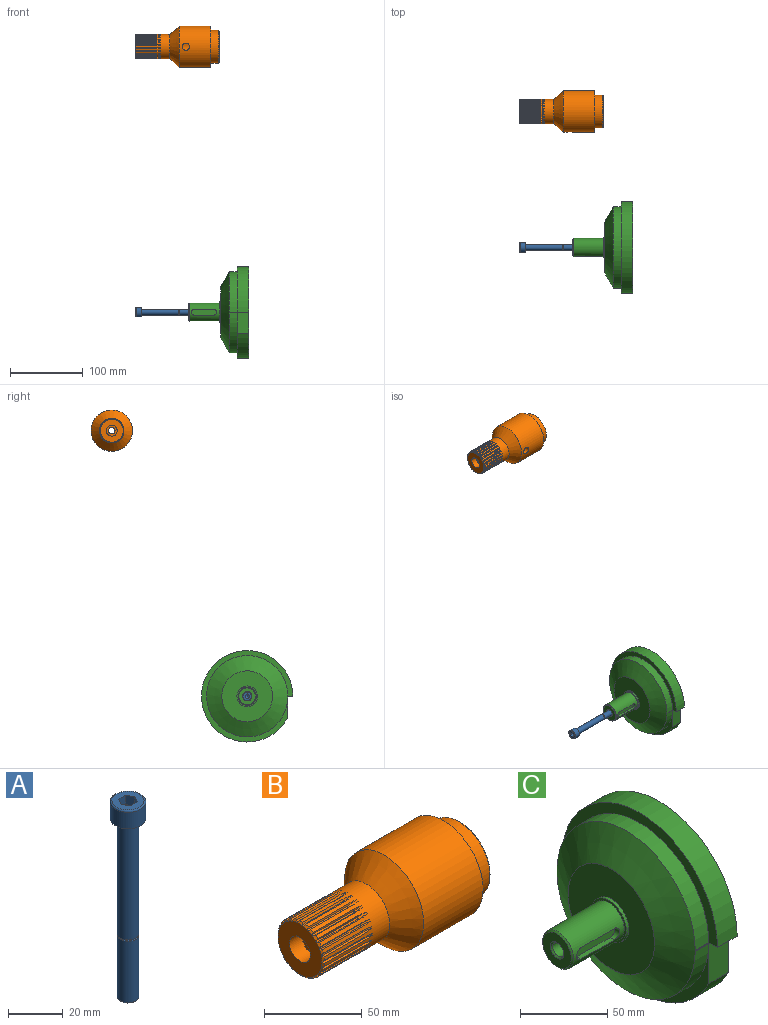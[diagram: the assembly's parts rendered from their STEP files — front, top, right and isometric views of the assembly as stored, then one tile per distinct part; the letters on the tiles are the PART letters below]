
ASSEMBLY  parts=3 mates=3
PART A: 17 faces, bbox 14.1x14.1x88 mm
  f0: cylinder r=6.5mm len=13mm, axis (0,0,-1), area 300.2mm2, adj f1,f16
  f1: torus R=5.85mm, axis (0,0,-1), area 40.2mm2, adj f0,f15
  f2: cone r=3.73mm half-angle=45deg, axis (0,0,1), area 17.9mm2, adj f3,f14
  f3: cylinder r=4mm len=27.46mm, axis (0,0,-1), area 690.1mm2, adj f2,f13
  f4: cone r=3.73mm half-angle=45deg, axis (0,0,1), area 17.9mm2, adj f5,f13
  f5: cylinder r=4mm len=51.46mm, axis (0,0,-1), area 1293.3mm2, adj f4,f16
  f6: cone r=1.73mm half-angle=60deg, axis (0,0,1), area 36mm2, adj f7,f8,f9,f10,f11,f12
  f7: plane 4.4x3mm, normal (0.87,0.5,0), area 14.5mm2, adj f6,f8,f12,f15
  f8: plane 4.4x3.46mm, normal (0,1,0), area 14.5mm2, adj f6,f7,f9,f15
  f9: plane 4.4x3mm, normal (-0.87,0.5,0), area 14.5mm2, adj f6,f8,f10,f15
  f10: plane 4.4x3mm, normal (-0.87,-0.5,0), area 14.5mm2, adj f6,f9,f11,f15
  f11: plane 4.31x3.46mm, normal (0,-1,0), area 14.5mm2, adj f6,f10,f12,f15
  f12: plane 4.4x3mm, normal (0.87,-0.5,0), area 14.5mm2, adj f6,f7,f11,f15
  f13: plane 8x8mm, normal (0,0,1), area 12.7mm2, adj f3,f4
  f14: plane 6.92x6.92mm, normal (0,0,-1), area 37.6mm2, adj f2
  f15: plane 11.7x11.7mm, normal (0,0,1), area 76.3mm2, adj f1,f7,f8,f9,f10,f11,f12
  f16: plane 13x13mm, normal (0,0,-1), area 82.5mm2, adj f0,f5
PART B: 200 faces, bbox 116x57x57 mm
  f0: cylinder r=12.5mm len=52.3mm, axis (-1,0,0), area 3694.3mm2, adj f2,f3,f36,f198,f199
  f1: cylinder r=28.5mm len=57mm, axis (-1,0,0), area 7621.6mm2, adj f32,f33,f198
  f2: plane 43.01x4.16mm, normal (0,-1,0), area 178.5mm2, adj f0,f35,f41,f198,f199
  f3: plane 43.01x4.16mm, normal (0,1,0), area 178.5mm2, adj f0,f35,f41,f198,f199
  f4: cone r=15.88mm half-angle=45deg, axis (1,0,0), area 3.5mm2, adj f30,f31,f177,f196
  f5: cone r=15.88mm half-angle=45deg, axis (1,0,0), area 3.5mm2, adj f30,f31,f190,f195
  f6: cone r=15.88mm half-angle=45deg, axis (1,0,0), area 3.5mm2, adj f30,f31,f87,f184
  f7: cone r=15.88mm half-angle=45deg, axis (1,0,0), area 3.5mm2, adj f30,f31,f178,f183
  f8: cone r=15.88mm half-angle=45deg, axis (1,0,0), area 3.5mm2, adj f30,f31,f153,f172
  f9: cone r=15.88mm half-angle=45deg, axis (1,0,0), area 3.5mm2, adj f30,f31,f166,f171
  f10: cone r=15.88mm half-angle=45deg, axis (1,0,0), area 3.5mm2, adj f30,f31,f160,f189
  f11: cone r=15.88mm half-angle=45deg, axis (1,0,0), area 3.5mm2, adj f30,f31,f154,f159
  f12: cone r=15.88mm half-angle=45deg, axis (1,0,0), area 3.5mm2, adj f30,f31,f141,f148
  f13: cone r=15.88mm half-angle=45deg, axis (1,0,0), area 3.5mm2, adj f30,f31,f123,f142
  f14: cone r=15.88mm half-angle=45deg, axis (1,0,0), area 3.5mm2, adj f30,f31,f129,f136
  f15: cone r=15.88mm half-angle=45deg, axis (1,0,0), area 3.5mm2, adj f30,f31,f130,f147
  f16: cone r=15.88mm half-angle=45deg, axis (1,0,0), area 3.5mm2, adj f30,f31,f117,f124
  f17: cone r=15.88mm half-angle=45deg, axis (1,0,0), area 3.5mm2, adj f30,f31,f105,f118
  f18: cone r=15.88mm half-angle=45deg, axis (1,0,0), area 3.5mm2, adj f30,f31,f112,f165
  f19: cone r=15.88mm half-angle=45deg, axis (1,0,0), area 3.5mm2, adj f30,f31,f106,f111
  f20: cone r=15.88mm half-angle=45deg, axis (1,0,0), area 3.5mm2, adj f30,f31,f45,f100
  f21: cone r=15.88mm half-angle=45deg, axis (1,0,0), area 3.5mm2, adj f30,f31,f81,f94
  f22: cone r=15.88mm half-angle=45deg, axis (1,0,0), area 3.5mm2, adj f30,f31,f88,f93
  f23: cone r=15.88mm half-angle=45deg, axis (1,0,0), area 3.5mm2, adj f30,f31,f75,f82
  f24: cone r=15.88mm half-angle=45deg, axis (1,0,0), area 3.5mm2, adj f30,f31,f57,f76
  f25: cone r=15.88mm half-angle=45deg, axis (1,0,0), area 3.5mm2, adj f30,f31,f63,f70
  f26: cone r=15.88mm half-angle=45deg, axis (1,0,0), area 3.5mm2, adj f30,f31,f64,f99
  f27: cone r=15.88mm half-angle=45deg, axis (1,0,0), area 3.5mm2, adj f30,f31,f51,f58
  f28: cone r=15.88mm half-angle=45deg, axis (1,0,0), area 3.5mm2, adj f30,f31,f52,f69
  f29: cylinder r=7.5mm len=15mm, axis (-1,0,0), area 424.1mm2, adj f30,f38
  f30: plane 31.75x31.75mm, normal (-1,0,0), area 615mm2, adj f4,f5,f6,f7,f8,f9,f10,f11
  f31: cylinder r=16.88mm len=47mm, axis (-1,0,0), area 3188.5mm2, adj f4,f5,f6,f7,f8,f9,f10,f11
  f32: cone r=28.5mm half-angle=41.8deg, axis (1,0,0), area 2486mm2, adj f1,f31
  f33: plane 57x57mm, normal (1,0,0), area 961.3mm2, adj f1,f34
  f34: cylinder r=22.5mm len=45mm, axis (-1,0,0), area 1555.1mm2, adj f33,f39
  f35: plane 43x43mm, normal (1,0,0), area 880.8mm2, adj f2,f3,f39,f41,f199
  f36: cone r=12.5mm half-angle=59deg, axis (1,0,0), area 498.5mm2, adj f0,f37
  f37: cylinder r=4.5mm len=49.19mm, axis (-1,0,0), area 1390.9mm2, adj f36,f38
  f38: plane 15x15mm, normal (-1,0,0), area 113.1mm2, adj f29,f37
  f39: cone r=22.5mm half-angle=45deg, axis (-1,0,0), area 195.5mm2, adj f34,f35
  f40: cone r=15.88mm half-angle=45deg, axis (1,0,0), area 3.5mm2, adj f30,f31,f46,f135
  f41: plane 43x8mm, normal (0,0,1), area 332.8mm2, adj f2,f3,f35,f198
  f42: cone r=15.3mm half-angle=59.4deg, axis (0,0.99,0.13), area 4.3mm2, adj f31,f44,f45
  f43: cone r=15.28mm half-angle=60.6deg, axis (0,-0.99,-0.13), area 4.3mm2, adj f31,f44,f46
  f44: torus R=32.14mm, axis (0,-0.99,-0.13), area 5.3mm2, adj f31,f42,f43,f47
  f45: plane 30.02x1.05mm, normal (0,0.92,-0.39), area 33.2mm2, adj f20,f31,f42,f47
  f46: plane 30.02x0.92mm, normal (0,-0.8,-0.6), area 33.2mm2, adj f31,f40,f43,f47
  f47: cylinder r=15.88mm len=30mm, axis (-1,0,0), area 27.8mm2, adj f30,f44,f45,f46
  f48: cone r=15.3mm half-angle=59.4deg, axis (0,0.67,-0.74), area 4.3mm2, adj f31,f50,f51
  f49: cone r=15.28mm half-angle=60.6deg, axis (0,-0.67,0.74), area 4.3mm2, adj f31,f50,f52
  f50: torus R=32.14mm, axis (0,-0.67,0.74), area 5.3mm2, adj f31,f48,f49,f53
  f51: plane 30.02x1.12mm, normal (0,0.2,-0.98), area 33.2mm2, adj f27,f31,f48,f53
  f52: plane 30.02x1.09mm, normal (0,-0.95,0.32), area 33.2mm2, adj f28,f31,f49,f53
  f53: cylinder r=15.88mm len=30mm, axis (-1,0,0), area 27.8mm2, adj f30,f50,f51,f52
  f54: cone r=15.3mm half-angle=59.4deg, axis (0,0.47,-0.88), area 4.3mm2, adj f31,f56,f57
  f55: cone r=15.28mm half-angle=60.6deg, axis (0,-0.47,0.88), area 4.3mm2, adj f31,f56,f58
  f56: torus R=32.14mm, axis (0,-0.47,0.88), area 5.3mm2, adj f31,f54,f55,f59
  f57: plane 30.02x1.14mm, normal (0,-0.04,-1), area 33.2mm2, adj f24,f31,f54,f59
  f58: plane 30.02x0.97mm, normal (0,-0.85,0.53), area 33.2mm2, adj f27,f31,f55,f59
  f59: cylinder r=15.88mm len=30mm, axis (-1,0,0), area 27.8mm2, adj f30,f56,f57,f58
  f60: cone r=15.3mm half-angle=59.4deg, axis (0,0.94,-0.34), area 4.3mm2, adj f31,f62,f63
  f61: cone r=15.28mm half-angle=60.6deg, axis (0,-0.94,0.34), area 4.3mm2, adj f31,f62,f64
  f62: torus R=32.14mm, axis (0,-0.94,0.34), area 5.3mm2, adj f31,f60,f61,f65
  f63: plane 30.02x0.89mm, normal (0,0.63,-0.77), area 33.2mm2, adj f25,f31,f60,f65
  f64: plane 30.02x1.13mm, normal (0,-0.99,-0.16), area 33.2mm2, adj f26,f31,f61,f65
  f65: cylinder r=15.88mm len=30mm, axis (-1,0,0), area 27.8mm2, adj f30,f62,f63,f64
  f66: cone r=15.3mm half-angle=59.4deg, axis (0,0.83,-0.56), area 4.3mm2, adj f31,f68,f69
  f67: cone r=15.28mm half-angle=60.6deg, axis (0,-0.83,0.56), area 4.3mm2, adj f31,f68,f70
  f68: torus R=32.14mm, axis (0,-0.83,0.56), area 5.3mm2, adj f31,f66,f67,f71
  f69: plane 30.02x1.03mm, normal (0,0.43,-0.9), area 33.2mm2, adj f28,f31,f66,f71
  f70: plane 30.02x1.14mm, normal (0,-1,0.08), area 33.2mm2, adj f25,f31,f67,f71
  f71: cylinder r=15.88mm len=30mm, axis (-1,0,0), area 27.8mm2, adj f30,f68,f69,f70
  f72: cone r=15.3mm half-angle=59.4deg, axis (0,0.25,-0.97), area 4.3mm2, adj f31,f74,f75
  f73: cone r=15.28mm half-angle=60.6deg, axis (0,-0.25,0.97), area 4.3mm2, adj f31,f74,f76
  f74: torus R=32.14mm, axis (0,-0.25,0.97), area 5.3mm2, adj f31,f72,f73,f77
  f75: plane 30.02x1.1mm, normal (0,-0.28,-0.96), area 33.2mm2, adj f23,f31,f72,f77
  f76: plane 30.02x0.83mm, normal (0,-0.69,0.72), area 33.2mm2, adj f24,f31,f73,f77
  f77: cylinder r=15.88mm len=30mm, axis (-1,0,0), area 27.8mm2, adj f30,f74,f75,f76
  f78: cone r=15.3mm half-angle=59.4deg, axis (0,0.01,-1), area 4.3mm2, adj f31,f80,f81
  f79: cone r=15.28mm half-angle=60.6deg, axis (0,-0.01,1), area 4.3mm2, adj f31,f80,f82
  f80: torus R=32.14mm, axis (0,-0.01,1), area 5.3mm2, adj f31,f78,f79,f83
  f81: plane 30.02x0.99mm, normal (0,-0.5,-0.87), area 33.2mm2, adj f21,f31,f78,f83
  f82: plane 30.02x0.99mm, normal (0,-0.5,0.87), area 33.2mm2, adj f23,f31,f79,f83
  f83: cylinder r=15.88mm len=30mm, axis (-1,0,0), area 27.8mm2, adj f30,f80,f81,f82
  f84: cone r=15.3mm half-angle=59.4deg, axis (0,-0.46,-0.89), area 4.3mm2, adj f31,f86,f87
  f85: cone r=15.28mm half-angle=60.6deg, axis (0,0.46,0.89), area 4.3mm2, adj f31,f86,f88
  f86: torus R=32.14mm, axis (0,0.46,0.89), area 5.3mm2, adj f31,f84,f85,f89
  f87: plane 30.02x0.97mm, normal (0,-0.85,-0.53), area 33.2mm2, adj f6,f31,f84,f89
  f88: plane 30.02x1.14mm, normal (0,-0.04,1), area 33.2mm2, adj f22,f31,f85,f89
  f89: cylinder r=15.88mm len=30mm, axis (-1,0,0), area 27.8mm2, adj f30,f86,f87,f88
  f90: cone r=15.3mm half-angle=59.4deg, axis (0,-0.23,-0.97), area 4.3mm2, adj f31,f92,f93
  f91: cone r=15.28mm half-angle=60.6deg, axis (0,0.23,0.97), area 4.3mm2, adj f31,f92,f94
  f92: torus R=32.14mm, axis (0,0.23,0.97), area 5.3mm2, adj f31,f90,f91,f95
  f93: plane 30.02x0.83mm, normal (0,-0.69,-0.72), area 33.2mm2, adj f22,f31,f90,f95
  f94: plane 30.02x1.1mm, normal (0,-0.28,0.96), area 33.2mm2, adj f21,f31,f91,f95
  f95: cylinder r=15.88mm len=30mm, axis (-1,0,0), area 27.8mm2, adj f30,f92,f93,f94
  f96: cone r=15.3mm half-angle=59.4deg, axis (0,0.99,-0.11), area 4.3mm2, adj f31,f98,f99
  f97: cone r=15.28mm half-angle=60.6deg, axis (0,-0.99,0.11), area 4.3mm2, adj f31,f98,f100
  f98: torus R=32.14mm, axis (0,-0.99,0.11), area 5.3mm2, adj f31,f96,f97,f101
  f99: plane 30.02x0.92mm, normal (0,0.8,-0.6), area 33.2mm2, adj f26,f31,f96,f101
  f100: plane 30.02x1.05mm, normal (0,-0.92,-0.39), area 33.2mm2, adj f20,f31,f97,f101
  f101: cylinder r=15.88mm len=30mm, axis (-1,0,0), area 27.8mm2, adj f30,f98,f99,f100
  f102: cone r=15.3mm half-angle=59.4deg, axis (0,-0.25,0.97), area 4.3mm2, adj f31,f104,f105
  f103: cone r=15.28mm half-angle=60.6deg, axis (0,0.25,-0.97), area 4.3mm2, adj f31,f104,f106
  f104: torus R=32.14mm, axis (0,0.25,-0.97), area 5.3mm2, adj f31,f102,f103,f107
  f105: plane 30.02x1.1mm, normal (0,0.28,0.96), area 33.2mm2, adj f17,f31,f102,f107
  f106: plane 30.02x0.83mm, normal (0,0.69,-0.72), area 33.2mm2, adj f19,f31,f103,f107
  f107: cylinder r=15.88mm len=30mm, axis (-1,0,0), area 27.8mm2, adj f30,f104,f105,f106
  f108: cone r=15.3mm half-angle=59.4deg, axis (0,-0.47,0.88), area 4.3mm2, adj f31,f110,f111
  f109: cone r=15.28mm half-angle=60.6deg, axis (0,0.47,-0.88), area 4.3mm2, adj f31,f110,f112
  f110: torus R=32.14mm, axis (0,0.47,-0.88), area 5.3mm2, adj f31,f108,f109,f113
  f111: plane 30.02x1.14mm, normal (0,0.04,1), area 33.2mm2, adj f19,f31,f108,f113
  f112: plane 30.02x0.97mm, normal (0,0.85,-0.53), area 33.2mm2, adj f18,f31,f109,f113
  f113: cylinder r=15.88mm len=30mm, axis (-1,0,0), area 27.8mm2, adj f30,f110,f111,f112
  f114: cone r=15.3mm half-angle=59.4deg, axis (0,-0.01,1), area 4.3mm2, adj f31,f116,f117
  f115: cone r=15.28mm half-angle=60.6deg, axis (0,0.01,-1), area 4.3mm2, adj f31,f116,f118
  f116: torus R=32.14mm, axis (0,0.01,-1), area 5.3mm2, adj f31,f114,f115,f119
  f117: plane 30.02x0.99mm, normal (0,0.5,0.87), area 33.2mm2, adj f16,f31,f114,f119
  f118: plane 30.02x0.99mm, normal (0,0.5,-0.87), area 33.2mm2, adj f17,f31,f115,f119
  f119: cylinder r=15.88mm len=30mm, axis (-1,0,0), area 27.8mm2, adj f30,f116,f117,f118
  f120: cone r=15.3mm half-angle=59.4deg, axis (0,0.23,0.97), area 4.3mm2, adj f31,f122,f123
  f121: cone r=15.28mm half-angle=60.6deg, axis (0,-0.23,-0.97), area 4.3mm2, adj f31,f122,f124
  f122: torus R=32.14mm, axis (0,-0.23,-0.97), area 5.3mm2, adj f31,f120,f121,f125
  f123: plane 30.02x0.83mm, normal (0,0.69,0.72), area 33.2mm2, adj f13,f31,f120,f125
  f124: plane 30.02x1.1mm, normal (0,0.28,-0.96), area 33.2mm2, adj f16,f31,f121,f125
  f125: cylinder r=15.88mm len=30mm, axis (-1,0,0), area 27.8mm2, adj f30,f122,f123,f124
  f126: cone r=15.3mm half-angle=59.4deg, axis (0,0.82,0.58), area 4.3mm2, adj f31,f128,f129
  f127: cone r=15.28mm half-angle=60.6deg, axis (0,-0.82,-0.58), area 4.3mm2, adj f31,f128,f130
  f128: torus R=32.14mm, axis (0,-0.82,-0.58), area 5.3mm2, adj f31,f126,f127,f131
  f129: plane 30.02x1.14mm, normal (0,1,0.08), area 33.2mm2, adj f14,f31,f126,f131
  f130: plane 30.02x1.03mm, normal (0,-0.43,-0.9), area 33.2mm2, adj f15,f31,f127,f131
  f131: cylinder r=15.88mm len=30mm, axis (-1,0,0), area 27.8mm2, adj f30,f128,f129,f130
  f132: cone r=15.3mm half-angle=59.4deg, axis (0,0.93,0.36), area 4.3mm2, adj f31,f134,f135
  f133: cone r=15.28mm half-angle=60.6deg, axis (0,-0.93,-0.36), area 4.3mm2, adj f31,f134,f136
  f134: torus R=32.14mm, axis (0,-0.93,-0.36), area 5.3mm2, adj f31,f132,f133,f137
  f135: plane 30.02x1.13mm, normal (0,0.99,-0.16), area 33.2mm2, adj f31,f40,f132,f137
  f136: plane 30.02x0.89mm, normal (0,-0.63,-0.77), area 33.2mm2, adj f14,f31,f133,f137
  f137: cylinder r=15.88mm len=30mm, axis (-1,0,0), area 27.8mm2, adj f30,f134,f135,f136
  f138: cone r=15.3mm half-angle=59.4deg, axis (0,0.46,0.89), area 4.3mm2, adj f31,f140,f141
  f139: cone r=15.28mm half-angle=60.6deg, axis (0,-0.46,-0.89), area 4.3mm2, adj f31,f140,f142
  f140: torus R=32.14mm, axis (0,-0.46,-0.89), area 5.3mm2, adj f31,f138,f139,f143
  f141: plane 30.02x0.97mm, normal (0,0.85,0.53), area 33.2mm2, adj f12,f31,f138,f143
  f142: plane 30.02x1.14mm, normal (0,0.04,-1), area 33.2mm2, adj f13,f31,f139,f143
  f143: cylinder r=15.88mm len=30mm, axis (-1,0,0), area 27.8mm2, adj f30,f140,f141,f142
  f144: cone r=15.3mm half-angle=59.4deg, axis (0,0.66,0.76), area 4.3mm2, adj f31,f146,f147
  f145: cone r=15.28mm half-angle=60.6deg, axis (0,-0.66,-0.76), area 4.3mm2, adj f31,f146,f148
  f146: torus R=32.14mm, axis (0,-0.66,-0.76), area 5.3mm2, adj f31,f144,f145,f149
  f147: plane 30.02x1.09mm, normal (0,0.95,0.32), area 33.2mm2, adj f15,f31,f144,f149
  f148: plane 30.02x1.12mm, normal (0,-0.2,-0.98), area 33.2mm2, adj f12,f31,f145,f149
  f149: cylinder r=15.88mm len=30mm, axis (-1,0,0), area 27.8mm2, adj f30,f146,f147,f148
  f150: cone r=15.3mm half-angle=59.4deg, axis (0,-0.94,0.34), area 4.3mm2, adj f31,f152,f153
  f151: cone r=15.28mm half-angle=60.6deg, axis (0,0.94,-0.34), area 4.3mm2, adj f31,f152,f154
  f152: torus R=32.14mm, axis (0,0.94,-0.34), area 5.3mm2, adj f31,f150,f151,f155
  f153: plane 30.02x0.89mm, normal (0,-0.63,0.77), area 33.2mm2, adj f8,f31,f150,f155
  f154: plane 30.02x1.13mm, normal (0,0.99,0.16), area 33.2mm2, adj f11,f31,f151,f155
  f155: cylinder r=15.88mm len=30mm, axis (-1,0,0), area 27.8mm2, adj f30,f152,f153,f154
  f156: cone r=15.3mm half-angle=59.4deg, axis (0,-0.99,0.11), area 4.3mm2, adj f31,f158,f159
  f157: cone r=15.28mm half-angle=60.6deg, axis (0,0.99,-0.11), area 4.3mm2, adj f31,f158,f160
  f158: torus R=32.14mm, axis (0,0.99,-0.11), area 5.3mm2, adj f31,f156,f157,f161
  f159: plane 30.02x0.92mm, normal (0,-0.8,0.6), area 33.2mm2, adj f11,f31,f156,f161
  f160: plane 30.02x1.05mm, normal (0,0.92,0.39), area 33.2mm2, adj f10,f31,f157,f161
  f161: cylinder r=15.88mm len=30mm, axis (-1,0,0), area 27.8mm2, adj f30,f158,f159,f160
  f162: cone r=15.3mm half-angle=59.4deg, axis (0,-0.67,0.74), area 4.3mm2, adj f31,f164,f165
  f163: cone r=15.28mm half-angle=60.6deg, axis (0,0.67,-0.74), area 4.3mm2, adj f31,f164,f166
  f164: torus R=32.14mm, axis (0,0.67,-0.74), area 5.3mm2, adj f31,f162,f163,f167
  f165: plane 30.02x1.12mm, normal (0,-0.2,0.98), area 33.2mm2, adj f18,f31,f162,f167
  f166: plane 30.02x1.09mm, normal (0,0.95,-0.32), area 33.2mm2, adj f9,f31,f163,f167
  f167: cylinder r=15.88mm len=30mm, axis (-1,0,0), area 27.8mm2, adj f30,f164,f165,f166
  f168: cone r=15.3mm half-angle=59.4deg, axis (0,-0.83,0.56), area 4.3mm2, adj f31,f170,f171
  f169: cone r=15.28mm half-angle=60.6deg, axis (0,0.83,-0.56), area 4.3mm2, adj f31,f170,f172
  f170: torus R=32.14mm, axis (0,0.83,-0.56), area 5.3mm2, adj f31,f168,f169,f173
  f171: plane 30.02x1.03mm, normal (0,-0.43,0.9), area 33.2mm2, adj f9,f31,f168,f173
  f172: plane 30.02x1.14mm, normal (0,1,-0.08), area 33.2mm2, adj f8,f31,f169,f173
  f173: cylinder r=15.88mm len=30mm, axis (-1,0,0), area 27.8mm2, adj f30,f170,f171,f172
  f174: cone r=15.3mm half-angle=59.4deg, axis (0,-0.82,-0.58), area 4.3mm2, adj f31,f176,f177
  f175: cone r=15.28mm half-angle=60.6deg, axis (0,0.82,0.58), area 4.3mm2, adj f31,f176,f178
  f176: torus R=32.14mm, axis (0,0.82,0.58), area 5.3mm2, adj f31,f174,f175,f179
  f177: plane 30.02x1.14mm, normal (0,-1,-0.08), area 33.2mm2, adj f4,f31,f174,f179
  f178: plane 30.02x1.03mm, normal (0,0.43,0.9), area 33.2mm2, adj f7,f31,f175,f179
  f179: cylinder r=15.88mm len=30mm, axis (-1,0,0), area 27.8mm2, adj f30,f176,f177,f178
  f180: cone r=15.3mm half-angle=59.4deg, axis (0,-0.66,-0.76), area 4.3mm2, adj f31,f182,f183
  f181: cone r=15.28mm half-angle=60.6deg, axis (0,0.66,0.76), area 4.3mm2, adj f31,f182,f184
  f182: torus R=32.14mm, axis (0,0.66,0.76), area 5.3mm2, adj f31,f180,f181,f185
  f183: plane 30.02x1.09mm, normal (0,-0.95,-0.32), area 33.2mm2, adj f7,f31,f180,f185
  f184: plane 30.02x1.12mm, normal (0,0.2,0.98), area 33.2mm2, adj f6,f31,f181,f185
  f185: cylinder r=15.88mm len=30mm, axis (-1,0,0), area 27.8mm2, adj f30,f182,f183,f184
  f186: cone r=15.3mm half-angle=59.4deg, axis (0,-0.99,-0.13), area 4.3mm2, adj f31,f188,f189
  f187: cone r=15.28mm half-angle=60.6deg, axis (0,0.99,0.13), area 4.3mm2, adj f31,f188,f190
  f188: torus R=32.14mm, axis (0,0.99,0.13), area 5.3mm2, adj f31,f186,f187,f191
  f189: plane 30.02x1.05mm, normal (0,-0.92,0.39), area 33.2mm2, adj f10,f31,f186,f191
  f190: plane 30.02x0.92mm, normal (0,0.8,0.6), area 33.2mm2, adj f5,f31,f187,f191
  f191: cylinder r=15.88mm len=30mm, axis (-1,0,0), area 27.8mm2, adj f30,f188,f189,f190
  f192: cone r=15.3mm half-angle=59.4deg, axis (0,-0.93,-0.36), area 4.3mm2, adj f31,f194,f195
  f193: cone r=15.28mm half-angle=60.6deg, axis (0,0.93,0.36), area 4.3mm2, adj f31,f194,f196
  f194: torus R=32.14mm, axis (0,0.93,0.36), area 5.3mm2, adj f31,f192,f193,f197
  f195: plane 30.02x1.13mm, normal (0,-0.99,0.16), area 33.2mm2, adj f5,f31,f192,f197
  f196: plane 30.02x0.89mm, normal (0,0.63,0.77), area 33.2mm2, adj f4,f31,f193,f197
  f197: cylinder r=15.88mm len=30mm, axis (-1,0,0), area 27.8mm2, adj f30,f194,f195,f196
  f198: cylinder r=5mm len=17.04mm, axis (0,0,-1), area 477.2mm2, adj f0,f1,f2,f3,f41
  f199: cone r=13.2mm half-angle=45deg, axis (1,0,0), area 71.9mm2, adj f0,f2,f3,f35
PART C: 21 faces, bbox 83x126x126 mm
  f0: plane 126x126mm, normal (1,0,0), area 12332.6mm2, adj f4,f19,f20
  f1: cone r=35mm half-angle=60.3deg, axis (1,0,0), area 6914.6mm2, adj f2,f9,f19,f20
  f2: cylinder r=56mm len=112mm, axis (-1,0,0), area 3861.9mm2, adj f1,f3,f19,f20
  f3: plane 126x126mm, normal (-1,0,0), area 2480.5mm2, adj f2,f4,f19,f20
  f4: cylinder r=63mm len=126mm, axis (-1,0,0), area 5853.6mm2, adj f0,f3,f19,f20
  f5: plane 23x23mm, normal (-1,0,0), area 320.4mm2, adj f10,f17
  f6: cylinder r=12.5mm len=41mm, axis (-1,0,0), area 2949.3mm2, adj f7,f10,f11,f12,f14,f15
  f7: plane 28.3x28.3mm, normal (-1,0,0), area 138.1mm2, adj f6,f8
  f8: cylinder r=14.15mm len=28.3mm, axis (-1,0,0), area 177.8mm2, adj f7,f9
  f9: plane 70x70mm, normal (-1,0,0), area 3219.4mm2, adj f1,f8
  f10: cone r=11.5mm half-angle=45deg, axis (1,0,0), area 106.6mm2, adj f5,f6
  f11: plane 27x3.34mm, normal (0,0,-1), area 90.3mm2, adj f6,f13,f14,f15
  f12: plane 27x3.34mm, normal (0,0,1), area 90.3mm2, adj f6,f13,f14,f15
  f13: plane 35x8mm, normal (0,-1,0), area 266.3mm2, adj f11,f12,f14,f15
  f14: cylinder r=4mm len=8mm, axis (0,-1,0), area 46.2mm2, adj f6,f11,f12,f13
  f15: cylinder r=4mm len=8mm, axis (0,-1,0), area 46.2mm2, adj f6,f11,f12,f13
  f16: cylinder r=4.5mm len=15mm, axis (-1,0,0), area 424.1mm2, adj f17,f18
  f17: cone r=4.5mm half-angle=45deg, axis (-1,0,0), area 44.4mm2, adj f5,f16
  f18: cone r=0mm half-angle=59deg, axis (-1,0,0), area 74.2mm2, adj f16
  f19: plane 28.88x27.01mm, normal (0,-1,0), area 470.5mm2, adj f0,f1,f2,f3,f4,f20
  f20: plane 27x7.01mm, normal (0,0,-1), area 112.1mm2, adj f0,f1,f2,f3,f4,f19
PLACE A rot(axis=(0,-1,0),90deg) t=(-41.87,45.81,12.75)mm
PLACE B rot(axis=(-1,0,0),90deg) t=(10.13,232.39,378.58)mm
PLACE C t=(23.13,33.31,12.75)mm fixed
MATE planar B.f0 <-> C.f1  axis (1,0,0) through (65.13,232.39,378.58)mm
MATE parallel C.f13 <-> B.f41  axis (0,-1,0) through (44.13,37.31,12.75)mm
MATE planar A.f4 <-> B.f0  axis (1,0,0) through (-41.87,45.81,12.75)mm
